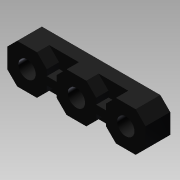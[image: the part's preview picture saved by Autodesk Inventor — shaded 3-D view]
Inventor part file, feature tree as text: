
AUTODESK INVENTOR PART (.ipt)
format: ipt  version: 2013 (Build 170138000, 138)  size: 225,792 bytes
history: native  units: mm (DEFAULTED — no unit token found)
features: extrude x7, sketch x6, other x3, chamfer x1, hole x1, pattern_linear x1
ambient origin geometry x8: Origin, YZ Plane, XZ Plane, XY Plane, X Axis, Y Axis, Z Axis, Center Point
bodies: Solid1 (feature_tree)
feature tree (19):
  extrude  "Extrusion1"  Depth=35.56mm
  chamfer  "Chamfer1"  Distance=3.175mm
  extrude  "Extrusion2"  Depth=10.16mm
  extrude  "Extrusion3"  Depth=2.54mm
  hole  "Hole1"  [1 undecoded]
  extrude  "Extrusion4"  Depth=2.54mm
  pattern_linear  "Rectangular Pattern1"  Spacing1=2.54mm  [1 undecoded]
  sketch  "Sketch1"  dims[d0=10.16mm d1=35.56mm d2=3.175mm d3=0.0mm]
  sketch  "Sketch2"  dims[d4=2.54mm d5=3.175mm d6=45.0deg d7=10.16mm]
  sketch  "Sketch3"  dims[d8=2.54mm d9=2.54mm]
  sketch  "Sketch4"  dims[d10=10.16mm d11=2.54mm]
  sketch  "Sketch5"  dims[d12=2.54mm d13=2.54mm]
  sketch  "Sketch6"  dims[d14=2.54mm d15=2.54mm d16=10.16mm d17=2.54mm d18=2.54mm d19=2.032mm d20=4.064mm d21=3.175mm d22=0.0mm d23=5.08mm d24=5.08mm d25=5.08mm d26=5.08mm d27=5.08mm d28=5.08mm d29=4.191mm d30=4.191mm d31=4.191mm d32=4.191mm d33=2.0955mm d34=2.0955mm d35=2.0955mm d36=2.0955mm d37=6.985mm d38=0.0mm d39=5.08mm d40=5.08mm d41=12.7mm d42=12.7mm d43=5.08mm d44=5.08mm d45=4.445mm d46=12.7mm d47=9.525mm d48=6.35mm d49=14.3117mm d50=19.05mm d51=20.594885mm d52=7.62mm d53=7.62mm d54=7.62mm d55=6.35mm d56=1.524mm d57=1.524mm d58=1.905mm d59=0.0mm d60=25.4mm d61=0.0mm d62=30.0mm d64=12.7mm d77=0.0mm d78=0.0mm d79=0.0mm d80=0.0mm d81=0.0mm d82=0.0mm]
  other  "Srf1"
  other  "Srf2"
  other  "Srf3"
  extrude  "ExtrusionSrf1"  Depth=10.16mm
  extrude  "ExtrusionSrf2"  Depth=2.54mm
  extrude  "ExtrusionSrf3"  Depth=2.54mm
note: 2 required parameter values undecoded (feature->parameter linkage not recoverable at this tier; creation-order binding heuristic only, values carry confidence <= 0.55)
